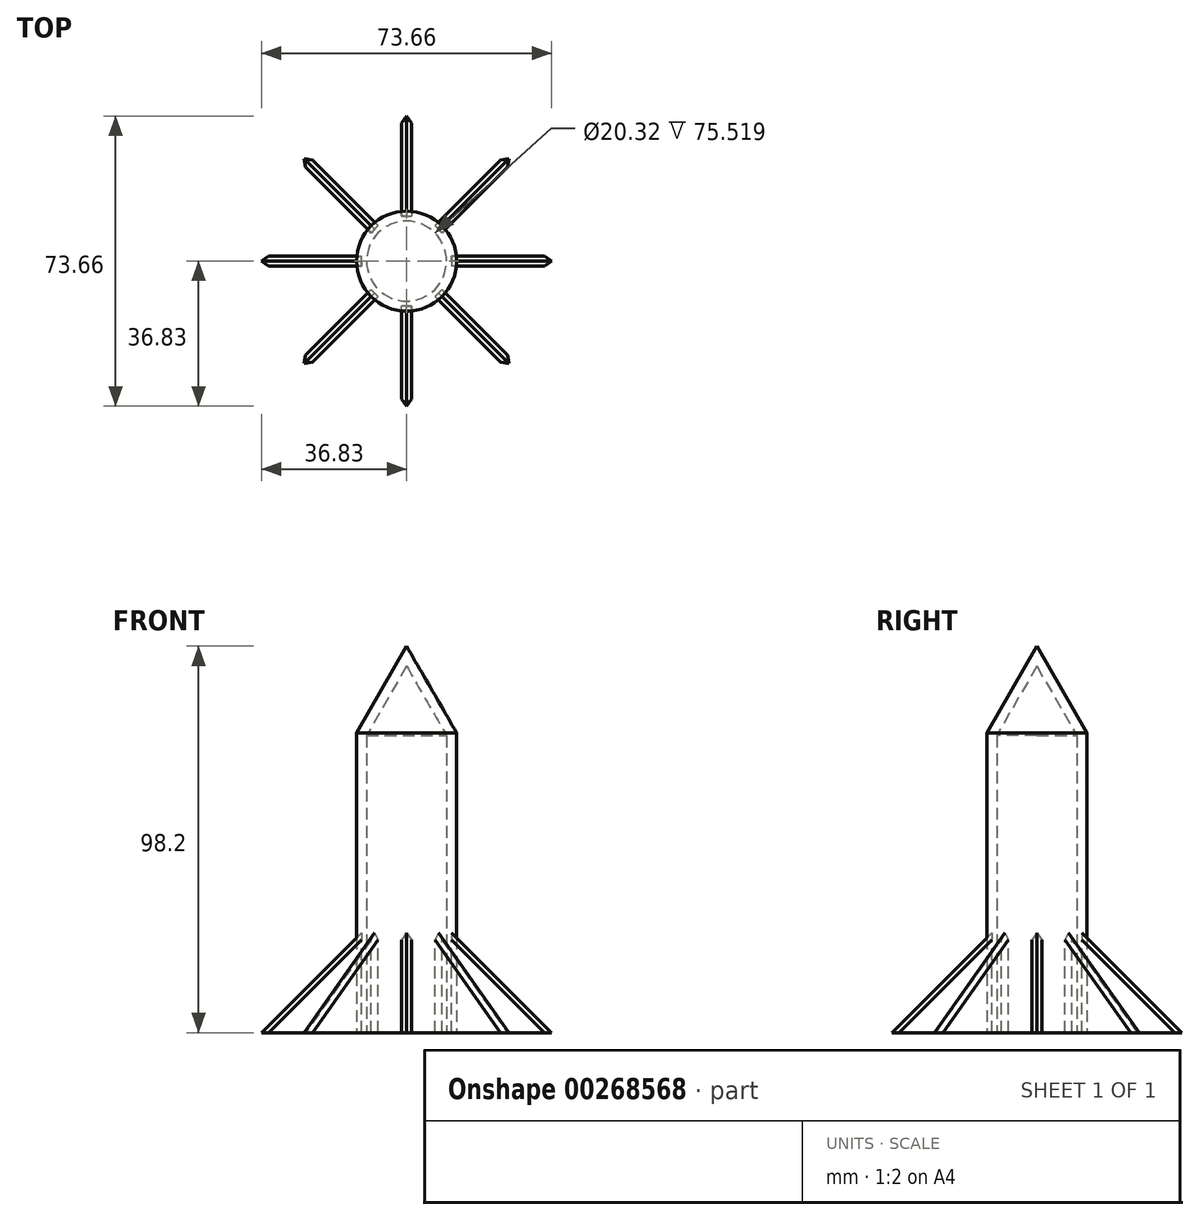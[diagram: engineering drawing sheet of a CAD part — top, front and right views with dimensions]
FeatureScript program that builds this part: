
annotation { "Feature Type Name" : "Feature", "Feature Type Description" : "" }
export const myFeature = defineFeature(function(context is Context, id is Id, definition is map)
    precondition{}
    {
        {
            var Q0;
            Q0=qCreatedBy(makeId("Top.planeOp"),FACE);
            var sketch = newSketch(context, id + "F0", { "sketchPlane" : qUnion([Q0])});
            skCircle(sketch, "E0", {"center": v(0, 0) * mm, "radius": 12.7 * mm});
            skSolve(sketch);
        }
        {
            var Q0;
            Q0 = qSketchRegion(id + "F0", true);
            extrude(context, id + "F1", {"entities" : qUnion([Q0]), "depth" : 76.2 * mm});
        }
        {
            var Q0;
            Q0=makeQuery(id+"F1.opExtrude","CAP_FACE",FACE,{"disambiguationData":[OSD([sQuery(id+"F0.wireOp",EDGE,"E0")])],"isStart":false});
            extrude(context, id + "F2", {"entities" : qUnion([Q0]), "operationType" : NewBodyOperationType.ADD, "depth" : 25.4 * mm, "hasDraft" : true, "draftAngle" : 30 * degree, "draftPullDirection" : true});
        }
        {
            var Q0;
            Q0=makeQuery(id+"F1.opExtrude","CAP_FACE",FACE,{"disambiguationData":[OSD([sQuery(id+"F0.wireOp",EDGE,"E0")])],"isStart":true});
            shell(context, id + "F3", {"entities" : qUnion([Q0]), "thickness" : 2.54 * mm});
        }
        {
            var Q0;
            Q0=qCreatedBy(makeId("Front.planeOp"),FACE);
            var sketch = newSketch(context, id + "F4", { "sketchPlane" : qUnion([Q0])});
            skLineSegment(sketch, "E1", {"start": v(-36.83, 0) * mm, "end": v(-11.43, 0) * mm});
            skLineSegment(sketch, "E2", {"start": v(-11.43, 0) * mm, "end": v(-11.43, 25.4) * mm});
            skLineSegment(sketch, "E3", {"start": v(-11.43, 25.4) * mm, "end": v(-36.83, 0) * mm});
            skSolve(sketch);
        }
        {
            var Q0;
            Q0 = qSketchRegion(id + "F4", true);
            extrude(context, id + "F5", {"entities" : qUnion([Q0]), "endBound" : BoundingType.SYMMETRIC, "depth" : 2.54 * mm});
        }
        {
            var Q0;
            Q0=makeQuery(id+"F5.opExtrude","CAP_EDGE",EDGE,{"disambiguationData":[OSD([sQuery(id+"F4.wireOp",EDGE,"E3")])],"isStart":false});
            var Q1;
            Q1=makeQuery(id+"F5.opExtrude","CAP_EDGE",EDGE,{"disambiguationData":[OSD([sQuery(id+"F4.wireOp",EDGE,"E3")])],"isStart":true});
            chamfer(context, id + "F6", {"entities" : qUnion([Q0, Q1]), "width" : 1.27 * mm, "tangentPropagation" : true});
        }
        {
            var Q0;
            Q0=makeQuery(id+"F5.opExtrude","SWEPT_BODY",BODY,{"disambiguationData":[OSD([sQuery(id+"F4.wireOp",EDGE,"E1"),sQuery(id+"F4.wireOp",EDGE,"E2"),sQuery(id+"F4.wireOp",EDGE,"E3")])]});
            var Q1;
            {var subQ0=sQuery(id+"F0.wireOp",EDGE,"E0");Q1=makeQuery(id+"F3.opShell","OFFSET_EDGE",EDGE,{"disambiguationData":[OSD([subQ0]),TDD([makeQuery(id+"F1.opExtrude","CAP_EDGE",EDGE,{"disambiguationData":[OSD([subQ0])],"isStart":true})])]});}
            circularPattern(context, id + "F7", {"entities" : qUnion([Q0]), "axis" : qUnion([Q1]), "angle" : 360 * degree, "instanceCount" : 8, "equalSpace" : true});
        }
    });
